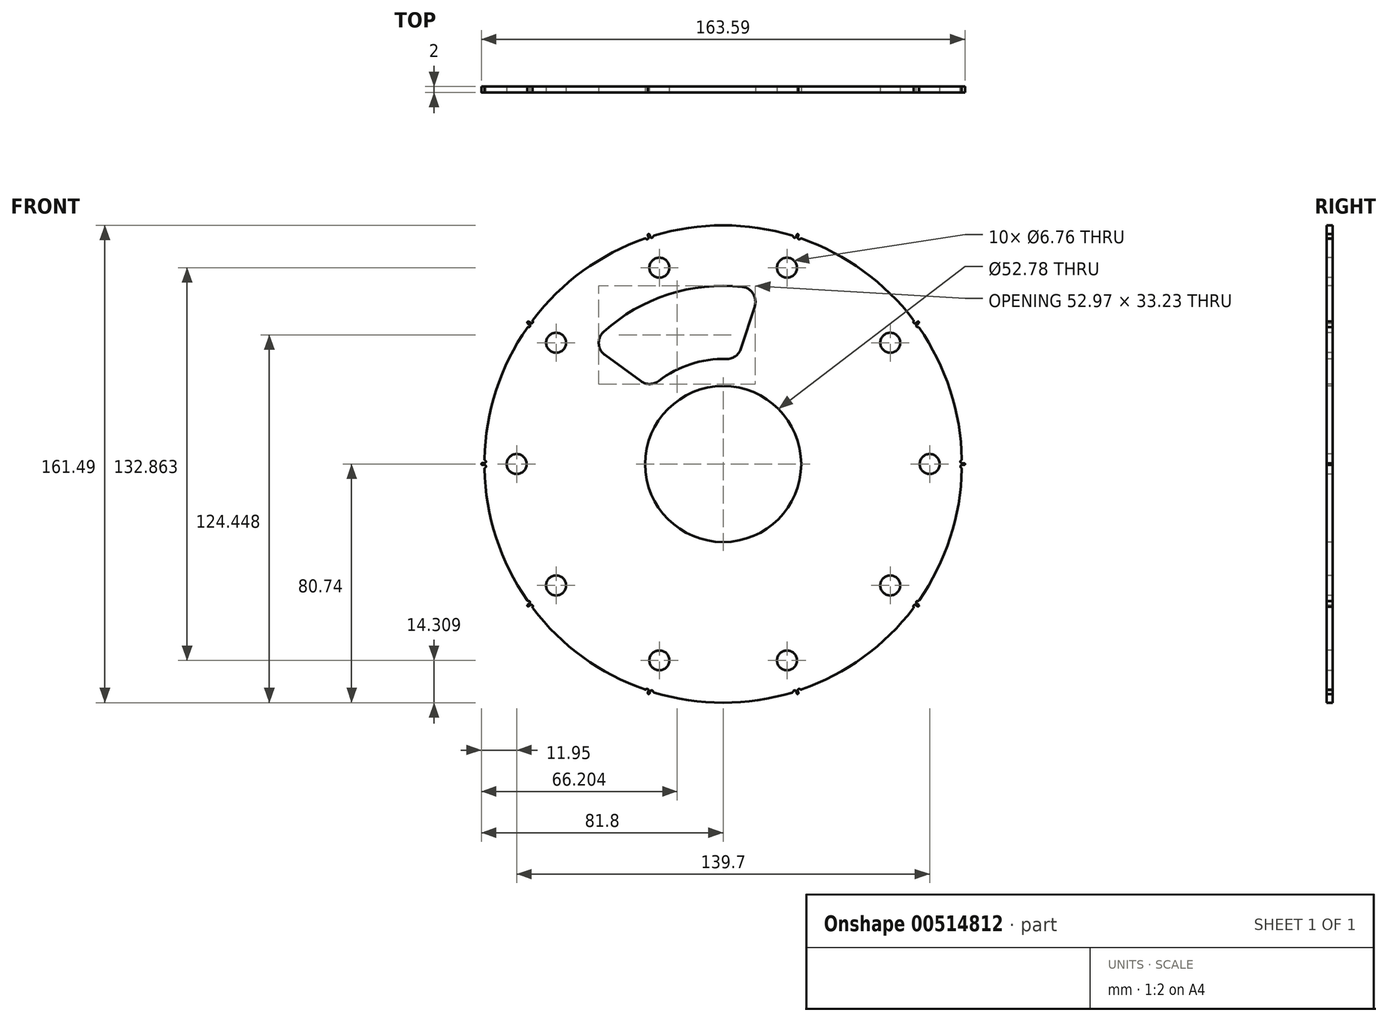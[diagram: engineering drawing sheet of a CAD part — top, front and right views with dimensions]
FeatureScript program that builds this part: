
annotation { "Feature Type Name" : "Feature", "Feature Type Description" : "" }
export const myFeature = defineFeature(function(context is Context, id is Id, definition is map)
    precondition{}
    {
        {
            var Q0;
            Q0=qCreatedBy(makeId("Front.planeOp"),FACE);
            var sketch = newSketch(context, id + "F0", { "sketchPlane" : qUnion([Q0])});
            skLineSegment(sketch, "E0", {"start": v(0, 0) * mm, "end": v(0, 59.02) * mm, "construction": true});
            skArc(sketch, "E1", {"start": v(24.79, 76.85) * mm, "mid": v(0, 80.75) * mm, "end": v(-24.79, 76.85) * mm, "construction": true});
            skArc(sketch, "E2.0", {"start": v(26, 85.9) * mm, "mid": v(0, 89.75) * mm, "end": v(-26, 85.9) * mm, "construction": true});
            skLineSegment(sketch, "E3", {"start": v(26, 85.9) * mm, "end": v(26, 80.62) * mm, "construction": true});
            skLineSegment(sketch, "E4.MirrorCS", {"start": v(-26, 80.62) * mm, "end": v(-24.79, 76.85) * mm, "construction": true});
            skLineSegment(sketch, "E5.MirrorCS", {"start": v(-26, 85.9) * mm, "end": v(-26, 80.62) * mm, "construction": true});
            skArc(sketch, "E6.1.0", {"start": v(-25.12, 76.74) * mm, "mid": v(-47.46, 65.33) * mm, "end": v(-65.22, 47.6) * mm, "construction": true});
            skArc(sketch, "E6.1.1", {"start": v(-29.46, 84.78) * mm, "mid": v(-52.75, 72.6) * mm, "end": v(-71.53, 54.21) * mm, "construction": true});
            skLineSegment(sketch, "E6.1.2", {"start": v(-71.53, 54.21) * mm, "end": v(-68.42, 49.94) * mm, "construction": true});
            skLineSegment(sketch, "E6.1.3", {"start": v(-68.42, 49.94) * mm, "end": v(-65.22, 47.6) * mm, "construction": true});
            skLineSegment(sketch, "E6.1.4", {"start": v(-29.46, 84.78) * mm, "end": v(-26.35, 80.5) * mm, "construction": true});
            skLineSegment(sketch, "E6.1.5", {"start": v(-26.35, 80.5) * mm, "end": v(-25.12, 76.74) * mm, "construction": true});
            skArc(sketch, "E6.2.0", {"start": v(-65.43, 47.32) * mm, "mid": v(-76.8, 24.95) * mm, "end": v(-80.75, 0.18) * mm, "construction": true});
            skArc(sketch, "E6.2.1", {"start": v(-73.66, 51.27) * mm, "mid": v(-85.36, 27.73) * mm, "end": v(-89.73, 1.82) * mm, "construction": true});
            skLineSegment(sketch, "E6.2.2", {"start": v(-89.73, 1.82) * mm, "end": v(-84.7, 0.18) * mm, "construction": true});
            skLineSegment(sketch, "E6.2.3", {"start": v(-84.7, 0.18) * mm, "end": v(-80.75, 0.18) * mm, "construction": true});
            skLineSegment(sketch, "E6.2.4", {"start": v(-73.66, 51.27) * mm, "end": v(-68.64, 49.64) * mm, "construction": true});
            skLineSegment(sketch, "E6.2.5", {"start": v(-68.64, 49.64) * mm, "end": v(-65.43, 47.32) * mm, "construction": true});
            skArc(sketch, "E6.3.0", {"start": v(-80.75, -0.18) * mm, "mid": v(-76.8, -24.95) * mm, "end": v(-65.43, -47.32) * mm, "construction": true});
            skArc(sketch, "E6.3.1", {"start": v(-89.73, -1.82) * mm, "mid": v(-85.36, -27.73) * mm, "end": v(-73.66, -51.27) * mm, "construction": true});
            skLineSegment(sketch, "E6.3.2", {"start": v(-73.66, -51.27) * mm, "end": v(-68.64, -49.64) * mm, "construction": true});
            skLineSegment(sketch, "E6.3.3", {"start": v(-68.64, -49.64) * mm, "end": v(-65.43, -47.32) * mm, "construction": true});
            skLineSegment(sketch, "E6.3.4", {"start": v(-89.73, -1.82) * mm, "end": v(-84.7, -0.18) * mm, "construction": true});
            skLineSegment(sketch, "E6.3.5", {"start": v(-84.7, -0.18) * mm, "end": v(-80.75, -0.18) * mm, "construction": true});
            skArc(sketch, "E6.4.0", {"start": v(-65.22, -47.6) * mm, "mid": v(-47.46, -65.33) * mm, "end": v(-25.12, -76.74) * mm, "construction": true});
            skArc(sketch, "E6.4.1", {"start": v(-71.53, -54.21) * mm, "mid": v(-52.75, -72.6) * mm, "end": v(-29.46, -84.78) * mm, "construction": true});
            skLineSegment(sketch, "E6.4.2", {"start": v(-29.46, -84.78) * mm, "end": v(-26.35, -80.5) * mm, "construction": true});
            skLineSegment(sketch, "E6.4.3", {"start": v(-26.35, -80.5) * mm, "end": v(-25.12, -76.74) * mm, "construction": true});
            skLineSegment(sketch, "E6.4.4", {"start": v(-71.53, -54.21) * mm, "end": v(-68.42, -49.94) * mm, "construction": true});
            skLineSegment(sketch, "E6.4.5", {"start": v(-68.42, -49.94) * mm, "end": v(-65.22, -47.6) * mm, "construction": true});
            skArc(sketch, "E6.5.0", {"start": v(-24.79, -76.85) * mm, "mid": v(0, -80.75) * mm, "end": v(24.79, -76.85) * mm, "construction": true});
            skArc(sketch, "E6.5.1", {"start": v(-26, -85.9) * mm, "mid": v(0, -89.75) * mm, "end": v(26, -85.9) * mm, "construction": true});
            skLineSegment(sketch, "E6.5.2", {"start": v(26, -85.9) * mm, "end": v(26, -80.62) * mm, "construction": true});
            skLineSegment(sketch, "E6.5.3", {"start": v(26, -80.62) * mm, "end": v(24.79, -76.85) * mm, "construction": true});
            skLineSegment(sketch, "E6.5.4", {"start": v(-26, -85.9) * mm, "end": v(-26, -80.62) * mm, "construction": true});
            skLineSegment(sketch, "E6.5.5", {"start": v(-26, -80.62) * mm, "end": v(-24.79, -76.85) * mm, "construction": true});
            skArc(sketch, "E6.6.0", {"start": v(25.12, -76.74) * mm, "mid": v(47.46, -65.33) * mm, "end": v(65.22, -47.6) * mm, "construction": true});
            skArc(sketch, "E6.6.1", {"start": v(29.46, -84.78) * mm, "mid": v(52.75, -72.6) * mm, "end": v(71.53, -54.21) * mm, "construction": true});
            skLineSegment(sketch, "E6.6.2", {"start": v(71.53, -54.21) * mm, "end": v(68.42, -49.94) * mm, "construction": true});
            skLineSegment(sketch, "E6.6.3", {"start": v(68.42, -49.94) * mm, "end": v(65.22, -47.6) * mm, "construction": true});
            skLineSegment(sketch, "E6.6.4", {"start": v(29.46, -84.78) * mm, "end": v(26.35, -80.5) * mm, "construction": true});
            skLineSegment(sketch, "E6.6.5", {"start": v(26.35, -80.5) * mm, "end": v(25.12, -76.74) * mm, "construction": true});
            skArc(sketch, "E6.7.0", {"start": v(65.43, -47.32) * mm, "mid": v(76.8, -24.95) * mm, "end": v(80.75, -0.18) * mm, "construction": true});
            skArc(sketch, "E6.7.1", {"start": v(73.66, -51.27) * mm, "mid": v(85.36, -27.73) * mm, "end": v(89.73, -1.82) * mm, "construction": true});
            skLineSegment(sketch, "E6.7.2", {"start": v(89.73, -1.82) * mm, "end": v(84.7, -0.18) * mm, "construction": true});
            skLineSegment(sketch, "E6.7.3", {"start": v(84.7, -0.18) * mm, "end": v(80.75, -0.18) * mm, "construction": true});
            skLineSegment(sketch, "E6.7.4", {"start": v(73.66, -51.27) * mm, "end": v(68.64, -49.64) * mm, "construction": true});
            skLineSegment(sketch, "E6.7.5", {"start": v(68.64, -49.64) * mm, "end": v(65.43, -47.32) * mm, "construction": true});
            skArc(sketch, "E6.8.0", {"start": v(80.75, 0.18) * mm, "mid": v(76.8, 24.95) * mm, "end": v(65.43, 47.32) * mm, "construction": true});
            skArc(sketch, "E6.8.1", {"start": v(89.73, 1.82) * mm, "mid": v(85.36, 27.73) * mm, "end": v(73.66, 51.27) * mm, "construction": true});
            skLineSegment(sketch, "E6.8.2", {"start": v(73.66, 51.27) * mm, "end": v(68.64, 49.64) * mm, "construction": true});
            skLineSegment(sketch, "E6.8.3", {"start": v(68.64, 49.64) * mm, "end": v(65.43, 47.32) * mm, "construction": true});
            skLineSegment(sketch, "E6.8.4", {"start": v(89.73, 1.82) * mm, "end": v(84.7, 0.18) * mm, "construction": true});
            skLineSegment(sketch, "E6.8.5", {"start": v(84.7, 0.18) * mm, "end": v(80.75, 0.18) * mm, "construction": true});
            skArc(sketch, "E6.9.0", {"start": v(65.22, 47.6) * mm, "mid": v(47.46, 65.33) * mm, "end": v(25.12, 76.74) * mm, "construction": true});
            skArc(sketch, "E6.9.1", {"start": v(71.53, 54.21) * mm, "mid": v(52.75, 72.6) * mm, "end": v(29.46, 84.78) * mm, "construction": true});
            skLineSegment(sketch, "E6.9.2", {"start": v(29.46, 84.78) * mm, "end": v(26.35, 80.5) * mm, "construction": true});
            skLineSegment(sketch, "E6.9.4", {"start": v(71.53, 54.21) * mm, "end": v(68.42, 49.94) * mm, "construction": true});
            skLineSegment(sketch, "E6.9.5", {"start": v(68.42, 49.94) * mm, "end": v(65.22, 47.6) * mm});
            skLineSegment(sketch, "E7", {"start": v(30.8, 94.8) * mm, "end": v(0, 0) * mm, "construction": true});
            skLineSegment(sketch, "E8", {"start": v(24.79, 76.85) * mm, "end": v(25.12, 76.74) * mm, "construction": true});
            skArc(sketch, "E9", {"start": v(23.36, 77.3) * mm, "mid": v(0, 80.75) * mm, "end": v(-23.36, 77.3) * mm});
            skPoint(sketch, "E10.center", {"position": v(0, -0.02) * mm});
            skPoint(sketch, "E11.visualSharp", {"position": v(23.83, 77.15) * mm});
            skPoint(sketch, "E12.newPointA", {"position": v(26.07, 76.43) * mm});
            skLineSegment(sketch, "E13.0", {"start": v(30.52, 94.9) * mm, "end": v(-0.29, 0.1) * mm, "construction": true});
            skLineSegment(sketch, "E14", {"start": v(24.67, 76.89) * mm, "end": v(24.95, 76.8) * mm, "construction": true});
            skLineSegment(sketch, "E15.0", {"start": v(24.9, 77.6) * mm, "end": v(25.18, 77.51) * mm, "construction": true});
            skLineSegment(sketch, "E16.MirrorCS", {"start": v(31.09, 94.7) * mm, "end": v(0.29, -0.1) * mm, "construction": true});
            skLineSegment(sketch, "E17.0", {"start": v(30.04, 95.04) * mm, "end": v(-0.76, 0.25) * mm, "construction": true});
            skArc(sketch, "E18.trimOffspring", {"start": v(25.47, 77.42) * mm, "mid": v(25.28, 77.8) * mm, "end": v(24.9, 77.6) * mm});
            skLineSegment(sketch, "E19", {"start": v(24.67, 76.89) * mm, "end": v(24.9, 77.6) * mm});
            skArc(sketch, "E20", {"start": v(24.67, 76.89) * mm, "mid": v(24.17, 76.54) * mm, "end": v(23.7, 76.93) * mm});
            skArc(sketch, "E21.MirrorCS", {"start": v(25.24, 76.7) * mm, "mid": v(25.43, 76.13) * mm, "end": v(26.04, 76.17) * mm});
            skPoint(sketch, "E22.newPointA", {"position": v(23.71, 77.19) * mm});
            skArc(sketch, "E22.filletArc", {"start": v(23.7, 76.93) * mm, "mid": v(23.58, 77.16) * mm, "end": v(23.36, 77.3) * mm});
            skPoint(sketch, "E23.visualSharp", {"position": v(26.19, 76.38) * mm});
            skLineSegment(sketch, "E24", {"start": v(25.24, 76.7) * mm, "end": v(25.47, 77.42) * mm});
            skArc(sketch, "E25.1.0", {"start": v(-26.53, 76.27) * mm, "mid": v(-47.46, 65.33) * mm, "end": v(-64.33, 48.8) * mm});
            skArc(sketch, "E25.1.1", {"start": v(-26.04, 76.17) * mm, "mid": v(-26.27, 76.29) * mm, "end": v(-26.53, 76.27) * mm});
            skArc(sketch, "E25.1.2", {"start": v(-25.24, 76.7) * mm, "mid": v(-25.44, 76.13) * mm, "end": v(-26.04, 76.17) * mm});
            skArc(sketch, "E25.1.3", {"start": v(-24.9, 77.6) * mm, "mid": v(-25.28, 77.8) * mm, "end": v(-25.47, 77.42) * mm});
            skLineSegment(sketch, "E25.1.4", {"start": v(-25.24, 76.7) * mm, "end": v(-25.47, 77.42) * mm});
            skLineSegment(sketch, "E25.1.5", {"start": v(-24.67, 76.9) * mm, "end": v(-24.9, 77.6) * mm});
            skArc(sketch, "E25.1.6", {"start": v(-24.67, 76.9) * mm, "mid": v(-24.17, 76.55) * mm, "end": v(-23.7, 76.93) * mm});
            skArc(sketch, "E25.2.0", {"start": v(-66.3, 46.11) * mm, "mid": v(-76.8, 24.96) * mm, "end": v(-80.73, 1.68) * mm});
            skArc(sketch, "E25.2.1", {"start": v(-65.84, 46.32) * mm, "mid": v(-66.1, 46.28) * mm, "end": v(-66.3, 46.11) * mm});
            skArc(sketch, "E25.2.2", {"start": v(-65.5, 47.23) * mm, "mid": v(-65.33, 46.65) * mm, "end": v(-65.84, 46.32) * mm});
            skArc(sketch, "E25.2.3", {"start": v(-65.76, 48.15) * mm, "mid": v(-66.18, 48.09) * mm, "end": v(-66.11, 47.67) * mm});
            skLineSegment(sketch, "E25.2.4", {"start": v(-65.5, 47.23) * mm, "end": v(-66.11, 47.67) * mm});
            skLineSegment(sketch, "E25.2.5", {"start": v(-65.15, 47.71) * mm, "end": v(-65.76, 48.15) * mm});
            skArc(sketch, "E25.2.6", {"start": v(-65.15, 47.71) * mm, "mid": v(-64.55, 47.72) * mm, "end": v(-64.4, 48.31) * mm});
            skArc(sketch, "E25.3.0", {"start": v(-80.74, -1.66) * mm, "mid": v(-76.8, -24.94) * mm, "end": v(-66.3, -46.1) * mm});
            skArc(sketch, "E25.3.1", {"start": v(-80.5, -1.22) * mm, "mid": v(-80.67, -1.4) * mm, "end": v(-80.74, -1.66) * mm});
            skArc(sketch, "E25.3.2", {"start": v(-80.75, -0.3) * mm, "mid": v(-80.27, -0.66) * mm, "end": v(-80.5, -1.22) * mm});
            skArc(sketch, "E25.3.3", {"start": v(-81.5, 0.3) * mm, "mid": v(-81.8, 0) * mm, "end": v(-81.5, -0.3) * mm});
            skLineSegment(sketch, "E25.3.4", {"start": v(-80.75, -0.3) * mm, "end": v(-81.5, -0.3) * mm});
            skLineSegment(sketch, "E25.3.5", {"start": v(-80.75, 0.3) * mm, "end": v(-81.5, 0.3) * mm});
            skArc(sketch, "E25.3.6", {"start": v(-80.75, 0.3) * mm, "mid": v(-80.27, 0.67) * mm, "end": v(-80.5, 1.24) * mm});
            skArc(sketch, "E25.4.0", {"start": v(-64.34, -48.8) * mm, "mid": v(-47.47, -65.32) * mm, "end": v(-26.54, -76.26) * mm});
            skArc(sketch, "E25.4.1", {"start": v(-64.4, -48.3) * mm, "mid": v(-64.44, -48.55) * mm, "end": v(-64.34, -48.8) * mm});
            skArc(sketch, "E25.4.2", {"start": v(-65.16, -47.7) * mm, "mid": v(-64.55, -47.7) * mm, "end": v(-64.4, -48.3) * mm});
            skArc(sketch, "E25.4.3", {"start": v(-66.12, -47.65) * mm, "mid": v(-66.19, -48.07) * mm, "end": v(-65.77, -48.14) * mm});
            skLineSegment(sketch, "E25.4.4", {"start": v(-65.16, -47.7) * mm, "end": v(-65.77, -48.14) * mm});
            skLineSegment(sketch, "E25.4.5", {"start": v(-65.51, -47.21) * mm, "end": v(-66.12, -47.65) * mm});
            skArc(sketch, "E25.4.6", {"start": v(-65.51, -47.21) * mm, "mid": v(-65.33, -46.63) * mm, "end": v(-65.85, -46.3) * mm});
            skArc(sketch, "E25.5.0", {"start": v(-23.37, -77.3) * mm, "mid": v(-0.01, -80.74) * mm, "end": v(23.35, -77.3) * mm});
            skArc(sketch, "E25.5.1", {"start": v(-23.72, -76.92) * mm, "mid": v(-23.6, -77.15) * mm, "end": v(-23.37, -77.3) * mm});
            skArc(sketch, "E25.5.2", {"start": v(-24.68, -76.88) * mm, "mid": v(-24.18, -76.54) * mm, "end": v(-23.72, -76.92) * mm});
            skArc(sketch, "E25.5.3", {"start": v(-25.48, -77.41) * mm, "mid": v(-25.29, -77.79) * mm, "end": v(-24.91, -77.6) * mm});
            skLineSegment(sketch, "E25.5.4", {"start": v(-24.68, -76.88) * mm, "end": v(-24.91, -77.6) * mm});
            skLineSegment(sketch, "E25.5.5", {"start": v(-25.25, -76.7) * mm, "end": v(-25.48, -77.41) * mm});
            skArc(sketch, "E25.5.6", {"start": v(-25.25, -76.7) * mm, "mid": v(-25.45, -76.12) * mm, "end": v(-26.05, -76.16) * mm});
            skArc(sketch, "E25.6.0", {"start": v(26.52, -76.26) * mm, "mid": v(47.45, -65.33) * mm, "end": v(64.32, -48.8) * mm});
            skArc(sketch, "E25.6.1", {"start": v(26.03, -76.17) * mm, "mid": v(26.26, -76.28) * mm, "end": v(26.52, -76.26) * mm});
            skArc(sketch, "E25.6.2", {"start": v(25.23, -76.7) * mm, "mid": v(25.42, -76.13) * mm, "end": v(26.03, -76.17) * mm});
            skArc(sketch, "E25.6.3", {"start": v(24.89, -77.6) * mm, "mid": v(25.26, -77.8) * mm, "end": v(25.46, -77.42) * mm});
            skLineSegment(sketch, "E25.6.4", {"start": v(25.23, -76.7) * mm, "end": v(25.46, -77.42) * mm});
            skLineSegment(sketch, "E25.6.5", {"start": v(24.66, -76.89) * mm, "end": v(24.89, -77.6) * mm});
            skArc(sketch, "E25.6.6", {"start": v(24.66, -76.89) * mm, "mid": v(24.16, -76.54) * mm, "end": v(23.7, -76.93) * mm});
            skArc(sketch, "E25.7.0", {"start": v(66.28, -46.1) * mm, "mid": v(76.79, -24.95) * mm, "end": v(80.72, -1.67) * mm});
            skArc(sketch, "E25.7.1", {"start": v(65.83, -46.32) * mm, "mid": v(66.09, -46.27) * mm, "end": v(66.28, -46.1) * mm});
            skArc(sketch, "E25.7.2", {"start": v(65.5, -47.22) * mm, "mid": v(65.32, -46.64) * mm, "end": v(65.83, -46.32) * mm});
            skArc(sketch, "E25.7.3", {"start": v(65.75, -48.15) * mm, "mid": v(66.17, -48.08) * mm, "end": v(66.1, -47.66) * mm});
            skLineSegment(sketch, "E25.7.4", {"start": v(65.5, -47.22) * mm, "end": v(66.1, -47.66) * mm});
            skLineSegment(sketch, "E25.7.5", {"start": v(65.14, -47.7) * mm, "end": v(65.75, -48.15) * mm});
            skArc(sketch, "E25.7.6", {"start": v(65.14, -47.7) * mm, "mid": v(64.53, -47.72) * mm, "end": v(64.38, -48.3) * mm});
            skArc(sketch, "E25.8.0", {"start": v(80.73, 1.67) * mm, "mid": v(76.8, 24.95) * mm, "end": v(66.29, 46.1) * mm});
            skArc(sketch, "E25.8.1", {"start": v(80.48, 1.23) * mm, "mid": v(80.66, 1.41) * mm, "end": v(80.73, 1.67) * mm});
            skArc(sketch, "E25.8.2", {"start": v(80.74, 0.3) * mm, "mid": v(80.26, 0.66) * mm, "end": v(80.48, 1.23) * mm});
            skArc(sketch, "E25.8.3", {"start": v(81.5, -0.3) * mm, "mid": v(81.8, 0) * mm, "end": v(81.5, 0.3) * mm});
            skLineSegment(sketch, "E25.8.4", {"start": v(80.74, 0.3) * mm, "end": v(81.5, 0.3) * mm});
            skLineSegment(sketch, "E25.8.5", {"start": v(80.74, -0.3) * mm, "end": v(81.5, -0.3) * mm});
            skArc(sketch, "E25.8.6", {"start": v(80.74, -0.3) * mm, "mid": v(80.26, -0.67) * mm, "end": v(80.48, -1.23) * mm});
            skArc(sketch, "E25.9.0", {"start": v(64.33, 48.8) * mm, "mid": v(47.46, 65.33) * mm, "end": v(26.53, 76.26) * mm});
            skArc(sketch, "E25.9.1", {"start": v(64.4, 48.3) * mm, "mid": v(64.43, 48.56) * mm, "end": v(64.33, 48.8) * mm});
            skArc(sketch, "E25.9.2", {"start": v(65.15, 47.7) * mm, "mid": v(64.54, 47.71) * mm, "end": v(64.4, 48.3) * mm});
            skArc(sketch, "E25.9.3", {"start": v(66.1, 47.66) * mm, "mid": v(66.17, 48.08) * mm, "end": v(65.76, 48.14) * mm});
            skLineSegment(sketch, "E25.9.4", {"start": v(65.15, 47.7) * mm, "end": v(65.76, 48.14) * mm});
            skLineSegment(sketch, "E25.9.5", {"start": v(65.5, 47.22) * mm, "end": v(66.1, 47.66) * mm});
            skArc(sketch, "E25.9.6", {"start": v(65.5, 47.22) * mm, "mid": v(65.32, 46.64) * mm, "end": v(65.83, 46.31) * mm});
            skPoint(sketch, "E26.orphan", {"position": v(-23.36, 77.3) * mm});
            skPoint(sketch, "E27.orphan", {"position": v(-23.7, 76.93) * mm});
            skArc(sketch, "E28.filletArc", {"start": v(-23.36, 77.3) * mm, "mid": v(-23.58, 77.16) * mm, "end": v(-23.7, 76.93) * mm});
            skPoint(sketch, "E29.newPointA", {"position": v(26.53, 76.26) * mm});
            skArc(sketch, "E29.filletArc", {"start": v(26.53, 76.26) * mm, "mid": v(26.27, 76.28) * mm, "end": v(26.04, 76.17) * mm});
            skPoint(sketch, "E30.orphan", {"position": v(-64.4, 48.3) * mm});
            skPoint(sketch, "E31.newPointB", {"position": v(-64.33, 48.8) * mm});
            skArc(sketch, "E31.filletArc", {"start": v(-64.33, 48.8) * mm, "mid": v(-64.43, 48.57) * mm, "end": v(-64.4, 48.31) * mm});
            skPoint(sketch, "E32.newPointB", {"position": v(-80.73, 1.68) * mm});
            skArc(sketch, "E32.filletArc", {"start": v(-80.73, 1.68) * mm, "mid": v(-80.67, 1.42) * mm, "end": v(-80.5, 1.24) * mm});
            skPoint(sketch, "E33.orphan", {"position": v(-65.84, -46.3) * mm});
            skPoint(sketch, "E34.newPointB", {"position": v(-66.3, -46.1) * mm});
            skArc(sketch, "E34.filletArc", {"start": v(-66.3, -46.1) * mm, "mid": v(-66.1, -46.26) * mm, "end": v(-65.85, -46.3) * mm});
            skPoint(sketch, "E35.orphan", {"position": v(-26.05, -76.16) * mm});
            skPoint(sketch, "E36.newPointB", {"position": v(-26.54, -76.26) * mm});
            skArc(sketch, "E36.filletArc", {"start": v(-26.54, -76.26) * mm, "mid": v(-26.28, -76.28) * mm, "end": v(-26.05, -76.16) * mm});
            skPoint(sketch, "E37.orphan", {"position": v(23.7, -76.92) * mm});
            skPoint(sketch, "E38.orphan", {"position": v(23.35, -77.3) * mm});
            skArc(sketch, "E39.filletArc", {"start": v(23.35, -77.3) * mm, "mid": v(23.57, -77.15) * mm, "end": v(23.7, -76.93) * mm});
            skPoint(sketch, "E40.orphan", {"position": v(64.38, -48.3) * mm});
            skPoint(sketch, "E41.orphan", {"position": v(64.32, -48.8) * mm});
            skArc(sketch, "E42.filletArc", {"start": v(64.32, -48.8) * mm, "mid": v(64.42, -48.56) * mm, "end": v(64.38, -48.3) * mm});
            skPoint(sketch, "E43.orphan", {"position": v(80.48, -1.23) * mm});
            skPoint(sketch, "E44.orphan", {"position": v(80.72, -1.67) * mm});
            skArc(sketch, "E45.filletArc", {"start": v(80.72, -1.67) * mm, "mid": v(80.66, -1.42) * mm, "end": v(80.48, -1.23) * mm});
            skPoint(sketch, "E46.orphan", {"position": v(65.83, 46.31) * mm});
            skPoint(sketch, "E47.orphan", {"position": v(66.29, 46.1) * mm});
            skArc(sketch, "E48.filletArc", {"start": v(66.29, 46.1) * mm, "mid": v(66.09, 46.27) * mm, "end": v(65.83, 46.31) * mm});
            skSolve(sketch);
        }
        {
            var Q0;
            Q0=makeQuery(id+"F0.imprint","IMPRINT",FACE,{"disambiguationData":[TD([[makeQuery(id+"F0.imprint","IMPRINT",EDGE,{"derivedFrom":sQuery(id+"F0.wireOp",EDGE,"E9")}),1.0]])]});
            extrude(context, id + "F1", {"entities" : qUnion([Q0]), "depth" : 2 * mm, "offsetDistance" : 25 * mm});
        }
        {
            var Q0;
            Q0=makeQuery(id+"F1.opExtrude","CAP_FACE",FACE,{"disambiguationData":[OSD([sQuery(id+"F0.wireOp",EDGE,"XIeMiUm1-8gPW-IMIm-pASV-yaVpRZOAZYnR"),sQuery(id+"F0.wireOp",EDGE,"Sk4poHVm-89H4-eliQ-Whh3-0xE3k8sZBWA0"),sQuery(id+"F0.wireOp",EDGE,"2de26b60-bd67-48f7-ae56-3656fd8014d00.MirrorCS"),sQuery(id+"F0.wireOp",EDGE,"JlpEmMME-SZbm-Hjtr-A6sC-niC8LgatfGaJ"),sQuery(id+"F0.wireOp",EDGE,"uWWTXu6I-KKbS-N7qE-Yg7B-Mz8SJ9bkHYqV"),sQuery(id+"F0.wireOp",EDGE,"E9"),sQuery(id+"F0.wireOp",EDGE,"E10.1.0"),sQuery(id+"F0.wireOp",EDGE,"E10.1.1"),sQuery(id+"F0.wireOp",EDGE,"E10.1.2"),sQuery(id+"F0.wireOp",EDGE,"E10.1.3"),sQuery(id+"F0.wireOp",EDGE,"E10.1.4"),sQuery(id+"F0.wireOp",EDGE,"E10.1.5"),sQuery(id+"F0.wireOp",EDGE,"E10.2.0"),sQuery(id+"F0.wireOp",EDGE,"E10.2.1"),sQuery(id+"F0.wireOp",EDGE,"E10.2.2"),sQuery(id+"F0.wireOp",EDGE,"E10.2.3"),sQuery(id+"F0.wireOp",EDGE,"E10.2.4"),sQuery(id+"F0.wireOp",EDGE,"E10.2.5"),sQuery(id+"F0.wireOp",EDGE,"E10.3.0"),sQuery(id+"F0.wireOp",EDGE,"E10.3.1"),sQuery(id+"F0.wireOp",EDGE,"E10.3.2"),sQuery(id+"F0.wireOp",EDGE,"E10.3.3"),sQuery(id+"F0.wireOp",EDGE,"E10.3.4"),sQuery(id+"F0.wireOp",EDGE,"E10.3.5"),sQuery(id+"F0.wireOp",EDGE,"E10.4.0"),sQuery(id+"F0.wireOp",EDGE,"E10.4.1"),sQuery(id+"F0.wireOp",EDGE,"E10.4.2"),sQuery(id+"F0.wireOp",EDGE,"E10.4.3"),sQuery(id+"F0.wireOp",EDGE,"E10.4.4"),sQuery(id+"F0.wireOp",EDGE,"E10.4.5"),sQuery(id+"F0.wireOp",EDGE,"E10.5.0"),sQuery(id+"F0.wireOp",EDGE,"E10.5.1"),sQuery(id+"F0.wireOp",EDGE,"E10.5.2"),sQuery(id+"F0.wireOp",EDGE,"E10.5.3"),sQuery(id+"F0.wireOp",EDGE,"E10.5.4"),sQuery(id+"F0.wireOp",EDGE,"E10.5.5"),sQuery(id+"F0.wireOp",EDGE,"E10.6.0"),sQuery(id+"F0.wireOp",EDGE,"E10.6.1"),sQuery(id+"F0.wireOp",EDGE,"E10.6.2"),sQuery(id+"F0.wireOp",EDGE,"E10.6.3"),sQuery(id+"F0.wireOp",EDGE,"E10.6.4"),sQuery(id+"F0.wireOp",EDGE,"E10.6.5"),sQuery(id+"F0.wireOp",EDGE,"E10.7.0"),sQuery(id+"F0.wireOp",EDGE,"E10.7.1"),sQuery(id+"F0.wireOp",EDGE,"E10.7.2"),sQuery(id+"F0.wireOp",EDGE,"E10.7.3"),sQuery(id+"F0.wireOp",EDGE,"E10.7.4"),sQuery(id+"F0.wireOp",EDGE,"E10.7.5"),sQuery(id+"F0.wireOp",EDGE,"E10.8.0"),sQuery(id+"F0.wireOp",EDGE,"E10.8.1"),sQuery(id+"F0.wireOp",EDGE,"E10.8.2"),sQuery(id+"F0.wireOp",EDGE,"E10.8.3"),sQuery(id+"F0.wireOp",EDGE,"E10.8.4"),sQuery(id+"F0.wireOp",EDGE,"E10.8.5"),sQuery(id+"F0.wireOp",EDGE,"E10.9.0"),sQuery(id+"F0.wireOp",EDGE,"E10.9.1"),sQuery(id+"F0.wireOp",EDGE,"E10.9.2"),sQuery(id+"F0.wireOp",EDGE,"E10.9.3"),sQuery(id+"F0.wireOp",EDGE,"E10.9.4"),sQuery(id+"F0.wireOp",EDGE,"E10.9.5")])],"isStart":false});
            var sketch = newSketch(context, id + "F2", { "sketchPlane" : qUnion([Q0])});
            skLineSegment(sketch, "E49", {"start": v(22.82, 70.22) * mm, "end": v(0, 0) * mm, "construction": true});
            skLineSegment(sketch, "E50", {"start": v(0, 0) * mm, "end": v(0, 83.92) * mm, "construction": true});
            skPoint(sketch, "E51.center", {"position": v(0, 0) * mm});
            skCircle(sketch, "E52", {"center": v(0, 0) * mm, "radius": 69.85 * mm, "construction": true});
            skPoint(sketch, "E53", {"position": v(21.58, 66.43) * mm});
            skPoint(sketch, "E54.1.0", {"position": v(-21.58, 66.43) * mm});
            skPoint(sketch, "E54.2.0", {"position": v(-56.5, 41.06) * mm});
            skPoint(sketch, "E54.3.0", {"position": v(-69.85, 0) * mm});
            skPoint(sketch, "E54.4.0", {"position": v(-56.5, -41.06) * mm});
            skPoint(sketch, "E54.5.0", {"position": v(-21.58, -66.43) * mm});
            skPoint(sketch, "E54.6.0", {"position": v(21.58, -66.43) * mm});
            skPoint(sketch, "E54.7.0", {"position": v(56.5, -41.06) * mm});
            skPoint(sketch, "E54.8.0", {"position": v(69.85, 0) * mm});
            skPoint(sketch, "E54.9.0", {"position": v(56.5, 41.06) * mm});
            skCircle(sketch, "E55", {"center": v(0, 0) * mm, "radius": 26.4 * mm});
            skSolve(sketch);
        }
        {
            var Q0;
            Q0=makeQuery(id+"F2.imprint","IMPRINT",FACE,{"disambiguationData":[TD([[makeQuery(id+"F2.imprint","IMPRINT",EDGE,{"derivedFrom":sQuery(id+"F2.wireOp",EDGE,"E55")}),1.0]])]});
            extrude(context, id + "F3", {"entities" : qUnion([Q0]), "operationType" : NewBodyOperationType.REMOVE, "endBound" : BoundingType.UP_TO_NEXT, "oppositeDirection" : true, "depth" : 25 * mm, "offsetDistance" : 25 * mm});
        }
        {
            var Q0;
            Q0=sQuery(id+"F2.wireOp",VERTEX,"E53");
            var Q1;
            Q1=sQuery(id+"F2.wireOp",VERTEX,"E54.1.0");
            var Q2;
            Q2=sQuery(id+"F2.wireOp",VERTEX,"E54.2.0");
            var Q3;
            Q3=sQuery(id+"F2.wireOp",VERTEX,"E54.3.0");
            var Q4;
            Q4=sQuery(id+"F2.wireOp",VERTEX,"E54.4.0");
            var Q5;
            Q5=sQuery(id+"F2.wireOp",VERTEX,"E54.5.0");
            var Q6;
            Q6=sQuery(id+"F2.wireOp",VERTEX,"E54.6.0");
            var Q7;
            Q7=sQuery(id+"F2.wireOp",VERTEX,"E54.7.0");
            var Q8;
            Q8=sQuery(id+"F2.wireOp",VERTEX,"E54.8.0");
            var Q9;
            Q9=sQuery(id+"F2.wireOp",VERTEX,"E54.9.0");
            var Q10;
            Q10=makeQuery(id+"F1.opExtrude","SWEPT_BODY",BODY,{"disambiguationData":[OSD([sQuery(id+"F0.wireOp",EDGE,"XIeMiUm1-8gPW-IMIm-pASV-yaVpRZOAZYnR"),sQuery(id+"F0.wireOp",EDGE,"Sk4poHVm-89H4-eliQ-Whh3-0xE3k8sZBWA0"),sQuery(id+"F0.wireOp",EDGE,"2de26b60-bd67-48f7-ae56-3656fd8014d00.MirrorCS"),sQuery(id+"F0.wireOp",EDGE,"JlpEmMME-SZbm-Hjtr-A6sC-niC8LgatfGaJ"),sQuery(id+"F0.wireOp",EDGE,"uWWTXu6I-KKbS-N7qE-Yg7B-Mz8SJ9bkHYqV"),sQuery(id+"F0.wireOp",EDGE,"E9"),sQuery(id+"F0.wireOp",EDGE,"E10.1.0"),sQuery(id+"F0.wireOp",EDGE,"E10.1.1"),sQuery(id+"F0.wireOp",EDGE,"E10.1.2"),sQuery(id+"F0.wireOp",EDGE,"E10.1.3"),sQuery(id+"F0.wireOp",EDGE,"E10.1.4"),sQuery(id+"F0.wireOp",EDGE,"E10.1.5"),sQuery(id+"F0.wireOp",EDGE,"E10.2.0"),sQuery(id+"F0.wireOp",EDGE,"E10.2.1"),sQuery(id+"F0.wireOp",EDGE,"E10.2.2"),sQuery(id+"F0.wireOp",EDGE,"E10.2.3"),sQuery(id+"F0.wireOp",EDGE,"E10.2.4"),sQuery(id+"F0.wireOp",EDGE,"E10.2.5"),sQuery(id+"F0.wireOp",EDGE,"E10.3.0"),sQuery(id+"F0.wireOp",EDGE,"E10.3.1"),sQuery(id+"F0.wireOp",EDGE,"E10.3.2"),sQuery(id+"F0.wireOp",EDGE,"E10.3.3"),sQuery(id+"F0.wireOp",EDGE,"E10.3.4"),sQuery(id+"F0.wireOp",EDGE,"E10.3.5"),sQuery(id+"F0.wireOp",EDGE,"E10.4.0"),sQuery(id+"F0.wireOp",EDGE,"E10.4.1"),sQuery(id+"F0.wireOp",EDGE,"E10.4.2"),sQuery(id+"F0.wireOp",EDGE,"E10.4.3"),sQuery(id+"F0.wireOp",EDGE,"E10.4.4"),sQuery(id+"F0.wireOp",EDGE,"E10.4.5"),sQuery(id+"F0.wireOp",EDGE,"E10.5.0"),sQuery(id+"F0.wireOp",EDGE,"E10.5.1"),sQuery(id+"F0.wireOp",EDGE,"E10.5.2"),sQuery(id+"F0.wireOp",EDGE,"E10.5.3"),sQuery(id+"F0.wireOp",EDGE,"E10.5.4"),sQuery(id+"F0.wireOp",EDGE,"E10.5.5"),sQuery(id+"F0.wireOp",EDGE,"E10.6.0"),sQuery(id+"F0.wireOp",EDGE,"E10.6.1"),sQuery(id+"F0.wireOp",EDGE,"E10.6.2"),sQuery(id+"F0.wireOp",EDGE,"E10.6.3"),sQuery(id+"F0.wireOp",EDGE,"E10.6.4"),sQuery(id+"F0.wireOp",EDGE,"E10.6.5"),sQuery(id+"F0.wireOp",EDGE,"E10.7.0"),sQuery(id+"F0.wireOp",EDGE,"E10.7.1"),sQuery(id+"F0.wireOp",EDGE,"E10.7.2"),sQuery(id+"F0.wireOp",EDGE,"E10.7.3"),sQuery(id+"F0.wireOp",EDGE,"E10.7.4"),sQuery(id+"F0.wireOp",EDGE,"E10.7.5"),sQuery(id+"F0.wireOp",EDGE,"E10.8.0"),sQuery(id+"F0.wireOp",EDGE,"E10.8.1"),sQuery(id+"F0.wireOp",EDGE,"E10.8.2"),sQuery(id+"F0.wireOp",EDGE,"E10.8.3"),sQuery(id+"F0.wireOp",EDGE,"E10.8.4"),sQuery(id+"F0.wireOp",EDGE,"E10.8.5"),sQuery(id+"F0.wireOp",EDGE,"E10.9.0"),sQuery(id+"F0.wireOp",EDGE,"E10.9.1"),sQuery(id+"F0.wireOp",EDGE,"E10.9.2"),sQuery(id+"F0.wireOp",EDGE,"E10.9.3"),sQuery(id+"F0.wireOp",EDGE,"E10.9.4"),sQuery(id+"F0.wireOp",EDGE,"E10.9.5")])]});
            hole(context, id + "F4", {"style" : HoleStyle.SIMPLE, "endStyle" : HoleEndStyle.THROUGH, "standardTappedOrClearance" : lookupTablePath({ "standard" : "ANSI", "fit" : "Normal (ASME)", "size" : "1/4", "type" : "Clearance" }), "standardBlindInLast" : lookupTablePath({ "fit" : "Free", "standard" : "ANSI", "size" : "1/4", "type" : "Clearance" }), "holeDiameter" : 6.76 * mm, "tappedDepth" : 25.4 * mm, "tapClearance" : 3, "startFromSketch" : true, "locations" : qUnion([Q0, Q1, Q2, Q3, Q4, Q5, Q6, Q7, Q8, Q9]), "scope" : qUnion([Q10])});
        }
        {
            var Q0;
            Q0=makeQuery(id+"F1.opExtrude","CAP_FACE",FACE,{"disambiguationData":[OSD([sQuery(id+"F0.wireOp",EDGE,"XIeMiUm1-8gPW-IMIm-pASV-yaVpRZOAZYnR"),sQuery(id+"F0.wireOp",EDGE,"Sk4poHVm-89H4-eliQ-Whh3-0xE3k8sZBWA0"),sQuery(id+"F0.wireOp",EDGE,"2de26b60-bd67-48f7-ae56-3656fd8014d00.MirrorCS"),sQuery(id+"F0.wireOp",EDGE,"JlpEmMME-SZbm-Hjtr-A6sC-niC8LgatfGaJ"),sQuery(id+"F0.wireOp",EDGE,"uWWTXu6I-KKbS-N7qE-Yg7B-Mz8SJ9bkHYqV"),sQuery(id+"F0.wireOp",EDGE,"E9"),sQuery(id+"F0.wireOp",EDGE,"E10.1.0"),sQuery(id+"F0.wireOp",EDGE,"E10.1.1"),sQuery(id+"F0.wireOp",EDGE,"E10.1.2"),sQuery(id+"F0.wireOp",EDGE,"E10.1.3"),sQuery(id+"F0.wireOp",EDGE,"E10.1.4"),sQuery(id+"F0.wireOp",EDGE,"E10.1.5"),sQuery(id+"F0.wireOp",EDGE,"E10.2.0"),sQuery(id+"F0.wireOp",EDGE,"E10.2.1"),sQuery(id+"F0.wireOp",EDGE,"E10.2.2"),sQuery(id+"F0.wireOp",EDGE,"E10.2.3"),sQuery(id+"F0.wireOp",EDGE,"E10.2.4"),sQuery(id+"F0.wireOp",EDGE,"E10.2.5"),sQuery(id+"F0.wireOp",EDGE,"E10.3.0"),sQuery(id+"F0.wireOp",EDGE,"E10.3.1"),sQuery(id+"F0.wireOp",EDGE,"E10.3.2"),sQuery(id+"F0.wireOp",EDGE,"E10.3.3"),sQuery(id+"F0.wireOp",EDGE,"E10.3.4"),sQuery(id+"F0.wireOp",EDGE,"E10.3.5"),sQuery(id+"F0.wireOp",EDGE,"E10.4.0"),sQuery(id+"F0.wireOp",EDGE,"E10.4.1"),sQuery(id+"F0.wireOp",EDGE,"E10.4.2"),sQuery(id+"F0.wireOp",EDGE,"E10.4.3"),sQuery(id+"F0.wireOp",EDGE,"E10.4.4"),sQuery(id+"F0.wireOp",EDGE,"E10.4.5"),sQuery(id+"F0.wireOp",EDGE,"E10.5.0"),sQuery(id+"F0.wireOp",EDGE,"E10.5.1"),sQuery(id+"F0.wireOp",EDGE,"E10.5.2"),sQuery(id+"F0.wireOp",EDGE,"E10.5.3"),sQuery(id+"F0.wireOp",EDGE,"E10.5.4"),sQuery(id+"F0.wireOp",EDGE,"E10.5.5"),sQuery(id+"F0.wireOp",EDGE,"E10.6.0"),sQuery(id+"F0.wireOp",EDGE,"E10.6.1"),sQuery(id+"F0.wireOp",EDGE,"E10.6.2"),sQuery(id+"F0.wireOp",EDGE,"E10.6.3"),sQuery(id+"F0.wireOp",EDGE,"E10.6.4"),sQuery(id+"F0.wireOp",EDGE,"E10.6.5"),sQuery(id+"F0.wireOp",EDGE,"E10.7.0"),sQuery(id+"F0.wireOp",EDGE,"E10.7.1"),sQuery(id+"F0.wireOp",EDGE,"E10.7.2"),sQuery(id+"F0.wireOp",EDGE,"E10.7.3"),sQuery(id+"F0.wireOp",EDGE,"E10.7.4"),sQuery(id+"F0.wireOp",EDGE,"E10.7.5"),sQuery(id+"F0.wireOp",EDGE,"E10.8.0"),sQuery(id+"F0.wireOp",EDGE,"E10.8.1"),sQuery(id+"F0.wireOp",EDGE,"E10.8.2"),sQuery(id+"F0.wireOp",EDGE,"E10.8.3"),sQuery(id+"F0.wireOp",EDGE,"E10.8.4"),sQuery(id+"F0.wireOp",EDGE,"E10.8.5"),sQuery(id+"F0.wireOp",EDGE,"E10.9.0"),sQuery(id+"F0.wireOp",EDGE,"E10.9.1"),sQuery(id+"F0.wireOp",EDGE,"E10.9.2"),sQuery(id+"F0.wireOp",EDGE,"E10.9.3"),sQuery(id+"F0.wireOp",EDGE,"E10.9.4"),sQuery(id+"F0.wireOp",EDGE,"E10.9.5")])],"isStart":false});
            var sketch = newSketch(context, id + "F5", { "sketchPlane" : qUnion([Q0])});
            skLineSegment(sketch, "E56", {"start": v(0, 0) * mm, "end": v(21.58, 66.43) * mm, "construction": true});
            skLineSegment(sketch, "E57", {"start": v(-56.5, 41.06) * mm, "end": v(0, 0) * mm, "construction": true});
            skLineSegment(sketch, "E58.0", {"start": v(-44.8, 40.4) * mm, "end": v(-24.57, 25.7) * mm});
            skCircle(sketch, "E59", {"center": v(0, 0) * mm, "radius": 60.33 * mm, "construction": true});
            skCircle(sketch, "E60", {"center": v(0, 0) * mm, "radius": 35.56 * mm, "construction": true});
            skArc(sketch, "E61", {"start": v(12.5, 59.02) * mm, "mid": v(-18.64, 57.37) * mm, "end": v(-44.8, 40.4) * mm});
            skArc(sketch, "E62", {"start": v(4.77, 35.24) * mm, "mid": v(-10.99, 33.82) * mm, "end": v(-24.57, 25.7) * mm});
            skLineSegment(sketch, "E63.trimOffspring", {"start": v(4.77, 35.24) * mm, "end": v(12.5, 59.02) * mm});
            skSolve(sketch);
        }
        {
            var Q0;
            Q0 = qSketchRegion(id + "F5", true);
            extrude(context, id + "F6", {"entities" : qUnion([Q0]), "operationType" : NewBodyOperationType.REMOVE, "endBound" : BoundingType.UP_TO_NEXT, "oppositeDirection" : true, "depth" : 25 * mm, "offsetDistance" : 25 * mm});
        }
        {
            var Q0;
            Q0=makeQuery(id+"F6.boolean.opBoolean","COPY",EDGE,{"derivedFrom":makeQuery(id+"F6.opExtrude","SWEPT_EDGE",EDGE,{"disambiguationData":[OSD([sQuery(id+"F5.wireOp",EDGE,"E58.0"),sQuery(id+"F5.wireOp",EDGE,"E61")])]})});
            var Q1;
            Q1=makeQuery(id+"F6.boolean.opBoolean","COPY",EDGE,{"derivedFrom":makeQuery(id+"F6.opExtrude","SWEPT_EDGE",EDGE,{"disambiguationData":[OSD([sQuery(id+"F5.wireOp",EDGE,"E58.0"),sQuery(id+"F5.wireOp",EDGE,"E62")])]})});
            var Q2;
            Q2=makeQuery(id+"F6.boolean.opBoolean","COPY",EDGE,{"derivedFrom":makeQuery(id+"F6.opExtrude","SWEPT_EDGE",EDGE,{"disambiguationData":[OSD([sQuery(id+"F5.wireOp",EDGE,"E62"),sQuery(id+"F5.wireOp",EDGE,"E63.trimOffspring")])]})});
            var Q3;
            Q3=makeQuery(id+"F6.boolean.opBoolean","COPY",EDGE,{"derivedFrom":makeQuery(id+"F6.opExtrude","SWEPT_EDGE",EDGE,{"disambiguationData":[OSD([sQuery(id+"F5.wireOp",EDGE,"E61"),sQuery(id+"F5.wireOp",EDGE,"E63.trimOffspring")])]})});
            fillet(context, id + "F7", {"entities" : qUnion([Q0, Q1, Q2, Q3]), "radius" : 5.08 * mm, "tangentPropagation" : true, "allowEdgeOverflow" : false});
        }
    });
